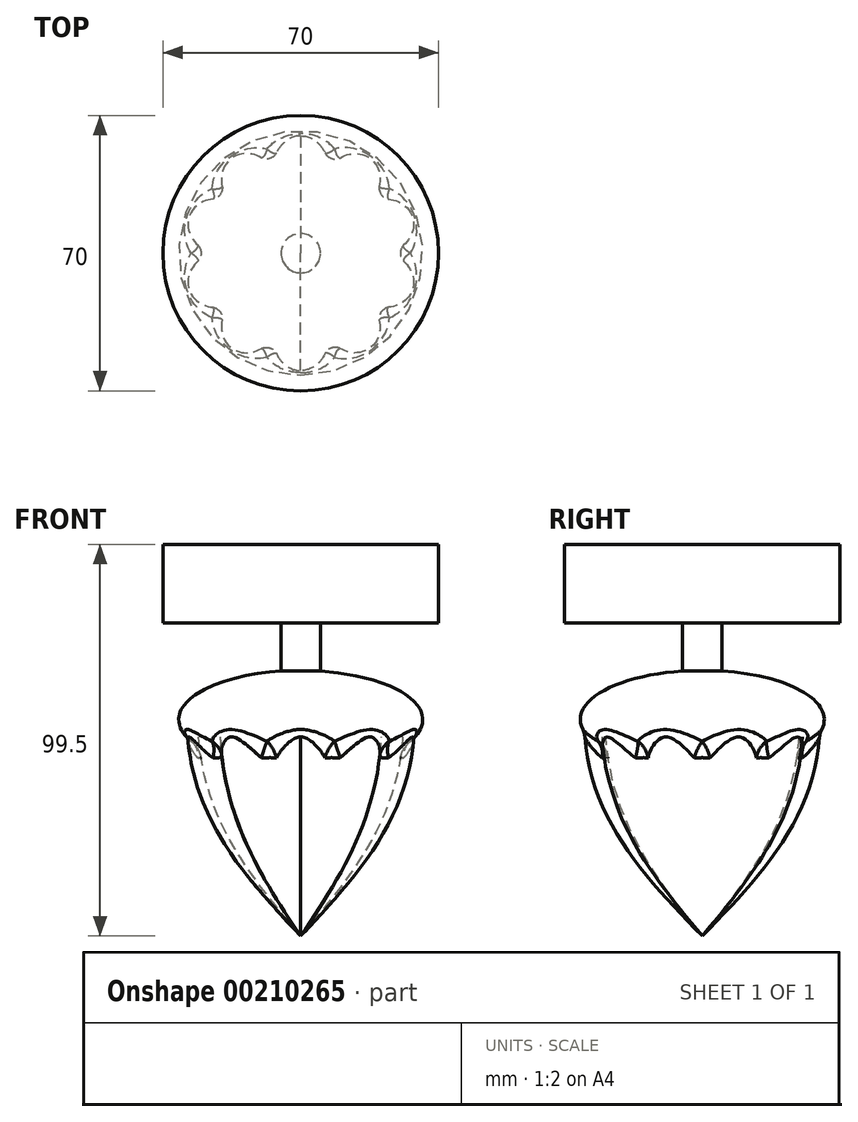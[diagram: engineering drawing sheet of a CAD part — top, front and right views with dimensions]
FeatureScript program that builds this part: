
annotation { "Feature Type Name" : "Feature", "Feature Type Description" : "" }
export const myFeature = defineFeature(function(context is Context, id is Id, definition is map)
    precondition{}
    {
        {
            var Q0;
            Q0=qCreatedBy(makeId("Top.planeOp"),FACE);
            var sketch = newSketch(context, id + "F0", { "sketchPlane" : qUnion([Q0])});
            skCircle(sketch, "E0", {"center": v(0, 0) * mm, "radius": 30 * mm});
            skCircle(sketch, "E1.cCircle", {"center": v(0, 0) * mm, "radius": 22 * mm, "construction": true});
            skLineSegment(sketch, "E1.0", {"start": v(-7.15, 22) * mm, "end": v(7.15, 22) * mm});
            skLineSegment(sketch, "E1.1", {"start": v(7.15, 22) * mm, "end": v(18.71, 13.6) * mm});
            skLineSegment(sketch, "E1.2", {"start": v(18.71, 13.6) * mm, "end": v(23.13, 0) * mm});
            skLineSegment(sketch, "E1.3", {"start": v(23.13, 0) * mm, "end": v(18.71, -13.6) * mm});
            skLineSegment(sketch, "E1.4", {"start": v(18.71, -13.6) * mm, "end": v(7.15, -22) * mm});
            skLineSegment(sketch, "E1.5", {"start": v(7.15, -22) * mm, "end": v(-7.15, -22) * mm});
            skLineSegment(sketch, "E1.6", {"start": v(-7.15, -22) * mm, "end": v(-18.71, -13.6) * mm});
            skLineSegment(sketch, "E1.7", {"start": v(-18.71, -13.6) * mm, "end": v(-23.13, 0) * mm});
            skLineSegment(sketch, "E1.8", {"start": v(-23.13, 0) * mm, "end": v(-18.71, 13.6) * mm});
            skLineSegment(sketch, "E1.9", {"start": v(-18.71, 13.6) * mm, "end": v(-7.15, 22) * mm});
            skPoint(sketch, "E1.0.midPoint", {"position": v(0, 22) * mm});
            skSolve(sketch);
        }
        {
            var Q0;
            Q0=qCreatedBy(makeId("Top.planeOp"),FACE);
            var sketch = newSketch(context, id + "F1", { "sketchPlane" : qUnion([Q0])});
            skArc(sketch, "E2", {"start": v(6.34, 26.21) * mm, "mid": v(0, 30) * mm, "end": v(-6.34, 26.21) * mm});
            skArc(sketch, "E3.1.0", {"start": v(-10.28, 24.93) * mm, "mid": v(-17.63, 24.27) * mm, "end": v(-20.53, 17.48) * mm});
            skArc(sketch, "E3.2.0", {"start": v(-22.97, 14.13) * mm, "mid": v(-28.53, 9.27) * mm, "end": v(-26.89, 2.07) * mm});
            skArc(sketch, "E3.3.0", {"start": v(-26.89, -2.07) * mm, "mid": v(-28.53, -9.27) * mm, "end": v(-22.97, -14.13) * mm});
            skArc(sketch, "E3.4.0", {"start": v(-20.53, -17.48) * mm, "mid": v(-17.63, -24.27) * mm, "end": v(-10.28, -24.93) * mm});
            skArc(sketch, "E3.5.0", {"start": v(-6.34, -26.21) * mm, "mid": v(0, -30) * mm, "end": v(6.34, -26.21) * mm});
            skArc(sketch, "E3.6.0", {"start": v(10.28, -24.93) * mm, "mid": v(17.63, -24.27) * mm, "end": v(20.53, -17.48) * mm});
            skArc(sketch, "E3.7.0", {"start": v(22.97, -14.13) * mm, "mid": v(28.53, -9.27) * mm, "end": v(26.89, -2.07) * mm});
            skArc(sketch, "E3.8.0", {"start": v(26.89, 2.07) * mm, "mid": v(28.53, 9.27) * mm, "end": v(22.97, 14.13) * mm});
            skArc(sketch, "E3.9.0", {"start": v(20.53, 17.48) * mm, "mid": v(17.63, 24.27) * mm, "end": v(10.28, 24.93) * mm});
            skPoint(sketch, "E3.center", {"position": v(0, 0) * mm});
            skPoint(sketch, "E4.visualSharp", {"position": v(7.15, 22) * mm});
            skArc(sketch, "E4.filletArc", {"start": v(6.34, 26.21) * mm, "mid": v(8.05, 24.78) * mm, "end": v(10.28, 24.93) * mm});
            skPoint(sketch, "E5.visualSharp", {"position": v(18.71, 13.6) * mm});
            skArc(sketch, "E5.filletArc", {"start": v(20.53, 17.48) * mm, "mid": v(21.08, 15.31) * mm, "end": v(22.97, 14.13) * mm});
            skPoint(sketch, "E6.visualSharp", {"position": v(23.13, 0) * mm});
            skArc(sketch, "E6.filletArc", {"start": v(26.89, 2.07) * mm, "mid": v(26.06, 0) * mm, "end": v(26.89, -2.07) * mm});
            skPoint(sketch, "E7.visualSharp", {"position": v(18.71, -13.6) * mm});
            skArc(sketch, "E7.filletArc", {"start": v(22.97, -14.13) * mm, "mid": v(21.08, -15.31) * mm, "end": v(20.53, -17.48) * mm});
            skPoint(sketch, "E8.visualSharp", {"position": v(7.15, -22) * mm});
            skArc(sketch, "E8.filletArc", {"start": v(10.28, -24.93) * mm, "mid": v(8.05, -24.78) * mm, "end": v(6.34, -26.21) * mm});
            skPoint(sketch, "E9.visualSharp", {"position": v(-7.15, -22) * mm});
            skArc(sketch, "E9.filletArc", {"start": v(-6.34, -26.21) * mm, "mid": v(-8.05, -24.78) * mm, "end": v(-10.28, -24.93) * mm});
            skPoint(sketch, "E10.visualSharp", {"position": v(-18.71, -13.6) * mm});
            skArc(sketch, "E10.filletArc", {"start": v(-20.53, -17.48) * mm, "mid": v(-21.08, -15.31) * mm, "end": v(-22.97, -14.13) * mm});
            skPoint(sketch, "E11.visualSharp", {"position": v(-23.13, 0) * mm});
            skArc(sketch, "E11.filletArc", {"start": v(-26.89, -2.07) * mm, "mid": v(-26.06, 0) * mm, "end": v(-26.89, 2.07) * mm});
            skPoint(sketch, "E12.visualSharp", {"position": v(-18.71, 13.6) * mm});
            skArc(sketch, "E12.filletArc", {"start": v(-22.97, 14.13) * mm, "mid": v(-21.08, 15.31) * mm, "end": v(-20.53, 17.48) * mm});
            skPoint(sketch, "E13.visualSharp", {"position": v(-7.15, 22) * mm});
            skArc(sketch, "E13.filletArc", {"start": v(-10.28, 24.93) * mm, "mid": v(-8.05, 24.78) * mm, "end": v(-6.34, 26.21) * mm});
            skSolve(sketch);
        }
        {
            var Q0;
            Q0=qCreatedBy(makeId("Right.planeOp"),FACE);
            var sketch = newSketch(context, id + "F2", { "sketchPlane" : qUnion([Q0])});
            skPoint(sketch, "E14", {"position": v(0, -55) * mm});
            skPoint(sketch, "E15", {"position": v(0, 55) * mm});
            skLineSegment(sketch, "E16", {"start": v(0, -55) * mm, "end": v(0, 0) * mm, "construction": true});
            skLineSegment(sketch, "E17", {"start": v(0, 0) * mm, "end": v(0, 55) * mm, "construction": true});
            skSolve(sketch);
        }
        {
            var Q0;
            Q0=sQuery(id+"F2.wireOp",VERTEX,"E14");
            var Q1;
            Q1=makeQuery(id+"F1.imprint","IMPRINT",FACE,{"disambiguationData":[TD([[makeQuery(id+"F1.imprint","IMPRINT",EDGE,{"derivedFrom":sQuery(id+"F1.wireOp",EDGE,"E2")}),1.0]])]});
            loft(context, id + "F3", {"endCondition" : LoftEndDerivativeType.NORMAL_TO_PROFILE, "endMagnitude" : 1.3, "sheetProfilesArray" : [{ "sheetProfileEntities" : qUnion([Q0]) }, { "sheetProfileEntities" : qUnion([Q1]) }]});
        }
        {
            var Q0;
            Q0=qCreatedBy(makeId("Right.planeOp"),FACE);
            var sketch = newSketch(context, id + "F4", { "sketchPlane" : qUnion([Q0])});
            skEllipticalArc(sketch, "E18", {});
            skLineSegment(sketch, "E19", {"start": v(0, 12.5) * mm, "end": v(0, -12.5) * mm});
            skPoint(sketch, "E20", {"position": v(-31, 0) * mm});
            const initialGuessF4  = {"E18": [0, 0, -1, 0, 0.031, 0.0125, 4.71238898038469, 1.5707963267948966]};
            skSetInitialGuess(sketch, initialGuessF4);
            skSolve(sketch);
        }
        {
            var Q0;
            Q0 = qSketchRegion(id + "F4", true);
            var Q1;
            Q1=sQuery(id+"F4.wireOp",EDGE,"E19");
            revolve(context, id + "F5", {"operationType" : NewBodyOperationType.ADD, "entities" : qUnion([Q0]), "axis" : qUnion([Q1]), "revolveType" : RevolveType.FULL});
        }
        {
            var Q0;
            Q0=makeQuery(id+"F5.boolean.opBoolean","INTERSECT",EDGE,{"derivedFrom":[makeQuery(id+"F3.opLoft","SWEPT_FACE",FACE,{"disambiguationData":[OSD([sQuery(id+"F1.wireOp",EDGE,"E3.4.0"),sQuery(id+"F1.wireOp",EDGE,"E3.5.0"),sQuery(id+"F1.wireOp",EDGE,"E9.filletArc")])]}),makeQuery(id+"F5.opRevolve","SWEPT_FACE",FACE,{"disambiguationData":[OSD([sQuery(id+"F4.wireOp",EDGE,"E18")])]})]});
            fillet(context, id + "F6", {"entities" : qUnion([Q0]), "radius" : 5 * mm, "tangentPropagation" : true, "allowEdgeOverflow" : false});
        }
        {
            var Q0;
            Q0=qCreatedBy(makeId("Right.planeOp"),FACE);
            var sketch = newSketch(context, id + "F7", { "sketchPlane" : qUnion([Q0])});
            skLineSegment(sketch, "E21.bottom", {"start": v(50.44, 29.16) * mm, "end": v(-60.9, 29.16) * mm});
            skLineSegment(sketch, "E21.top", {"start": v(50.44, -69.44) * mm, "end": v(-60.9, -69.44) * mm});
            skLineSegment(sketch, "E21.left", {"start": v(50.44, 29.16) * mm, "end": v(50.44, -69.44) * mm});
            skLineSegment(sketch, "E21.right", {"start": v(-60.9, 29.16) * mm, "end": v(-60.9, -69.44) * mm});
            skSolve(sketch);
        }
        {
            var Q0;
            Q0 = qSketchRegion(id + "F7", true);
            extrude(context, id + "F8", {"entities" : qUnion([Q0]), "operationType" : NewBodyOperationType.REMOVE, "endBound" : BoundingType.THROUGH_ALL, "oppositeDirection" : true, "depth" : 25 * mm});
        }
        {
            var Q0;
            Q0=makeQuery(id+"F8.boolean.opBoolean","COPY",FACE,{"derivedFrom":makeQuery(id+"F8.opExtrude","CAP_FACE",FACE,{"disambiguationData":[OSD([sQuery(id+"F7.wireOp",EDGE,"E21.bottom"),sQuery(id+"F7.wireOp",EDGE,"E21.top"),sQuery(id+"F7.wireOp",EDGE,"E21.left"),sQuery(id+"F7.wireOp",EDGE,"E21.right")])],"isStart":true})});
            var sketch = newSketch(context, id + "F9", { "sketchPlane" : qUnion([Q0])});
            skLineSegment(sketch, "E22.bottom", {"start": v(0, 0) * mm, "end": v(5, 0) * mm});
            skLineSegment(sketch, "E22.top", {"start": v(0, 24.5) * mm, "end": v(5, 24.5) * mm});
            skLineSegment(sketch, "E22.left", {"start": v(0, 0) * mm, "end": v(0, 24.5) * mm});
            skLineSegment(sketch, "E22.right", {"start": v(5, 0) * mm, "end": v(5, 24.5) * mm});
            skPoint(sketch, "E23", {"position": v(0, 12.5) * mm});
            skSolve(sketch);
        }
        {
            var Q0;
            Q0 = qSketchRegion(id + "F9", true);
            var Q1;
            Q1=sQuery(id+"F9.wireOp",EDGE,"E22.left");
            revolve(context, id + "F10", {"operationType" : NewBodyOperationType.ADD, "entities" : qUnion([Q0]), "axis" : qUnion([Q1]), "revolveType" : RevolveType.ONE_DIRECTION, "angle" : 180 * degree});
        }
        {
            var Q0;
            Q0=makeQuery(id+"F3.opLoft","SWEPT_BODY",BODY,{"disambiguationData":[OSD([makeQuery(id+"F1.imprint","IMPRINT",FACE,{"disambiguationData":[TD([[makeQuery(id+"F1.imprint","IMPRINT",EDGE,{"derivedFrom":sQuery(id+"F1.wireOp",EDGE,"E2")}),1.0]])]}),sQuery(id+"F2.wireOp",VERTEX,"E14")])]});
            var Q1;
            Q1=makeQuery(id+"F10.boolean.opBoolean","MERGE",FACE,{"derivedFrom":[makeQuery(id+"F8.boolean.opBoolean","COPY",FACE,{"derivedFrom":makeQuery(id+"F8.opExtrude","CAP_FACE",FACE,{"disambiguationData":[OSD([sQuery(id+"F7.wireOp",EDGE,"E21.bottom"),sQuery(id+"F7.wireOp",EDGE,"E21.top"),sQuery(id+"F7.wireOp",EDGE,"E21.left"),sQuery(id+"F7.wireOp",EDGE,"E21.right")])],"isStart":true})}),makeQuery(id+"F10.opRevolve","CAP_FACE",FACE,{"disambiguationData":[OSD([sQuery(id+"F9.wireOp",EDGE,"E22.bottom"),sQuery(id+"F9.wireOp",EDGE,"E22.top"),sQuery(id+"F9.wireOp",EDGE,"E22.left"),sQuery(id+"F9.wireOp",EDGE,"E22.right")])],"isStart":false})]});
            mirror(context, id + "F11", {"operationType" : NewBodyOperationType.ADD, "entities" : qUnion([Q0]), "mirrorPlane" : qUnion([Q1])});
        }
        {
            var Q0;
            Q0=qCreatedBy(makeId("Right.planeOp"),FACE);
            var sketch = newSketch(context, id + "F12", { "sketchPlane" : qUnion([Q0])});
            skLineSegment(sketch, "E24.bottom", {"start": v(0, 24.5) * mm, "end": v(35, 24.5) * mm});
            skLineSegment(sketch, "E24.top", {"start": v(0, 44.5) * mm, "end": v(35, 44.5) * mm});
            skLineSegment(sketch, "E24.left", {"start": v(0, 24.5) * mm, "end": v(0, 44.5) * mm});
            skLineSegment(sketch, "E24.right", {"start": v(35, 24.5) * mm, "end": v(35, 44.5) * mm});
            skSolve(sketch);
        }
        {
            var Q0;
            Q0 = qSketchRegion(id + "F12", true);
            var Q1;
            Q1=sQuery(id+"F12.wireOp",EDGE,"E24.left");
            revolve(context, id + "F13", {"operationType" : NewBodyOperationType.ADD, "entities" : qUnion([Q0]), "axis" : qUnion([Q1]), "revolveType" : RevolveType.FULL});
        }
    });
